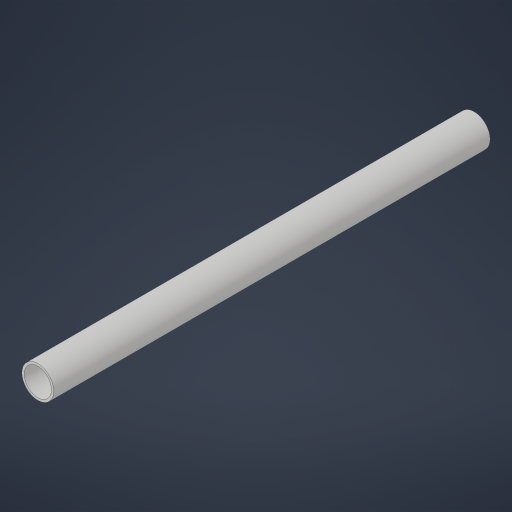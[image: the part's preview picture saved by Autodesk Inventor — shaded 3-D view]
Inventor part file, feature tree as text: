
AUTODESK INVENTOR PART (.ipt)
format: ipt  version: 2023.4 (Build 274418000, 418)  size: 164,864 bytes
history: native  units: in
note: dims shown in document units (in); Inventor stores cm internally (conversion verified against a paired STEP export)
features: extrude x1, sketch x1
ambient origin geometry x8: Origin, YZ Plane, XZ Plane, XY Plane, X Axis, Y Axis, Z Axis, Center Point
bodies: Solid1 (feature_tree)
feature tree (2):
  extrude  "Extrusion1"  Depth=12.0in TaperAngle=0.0deg
  sketch  "Sketch1"  dims[d0=0.875in d1=12.0in d2=0.0in d3=0.0625in]
